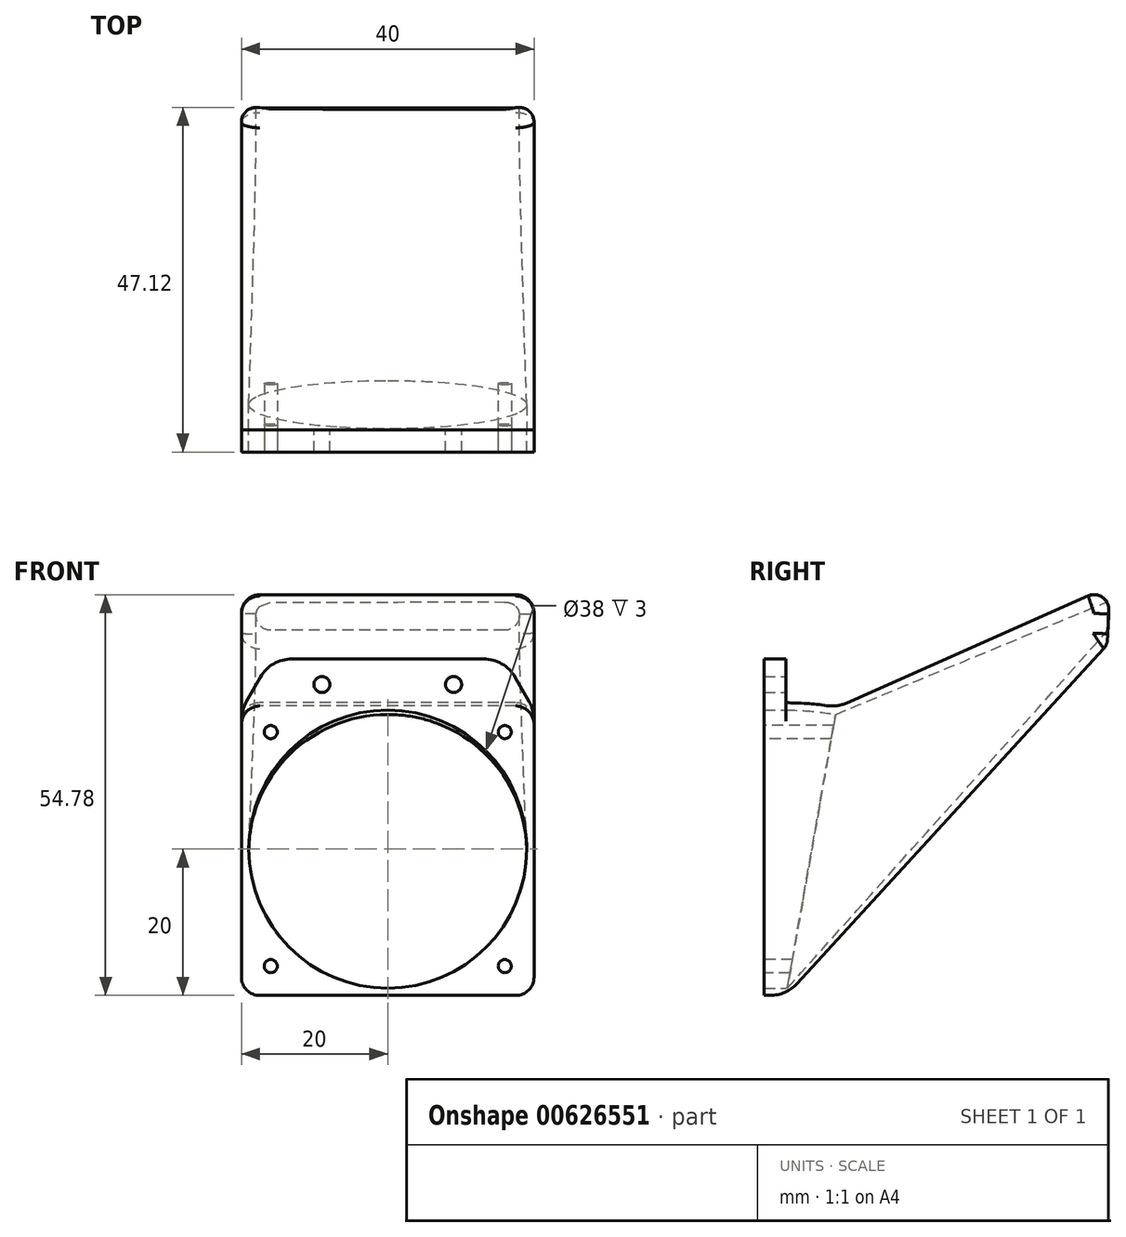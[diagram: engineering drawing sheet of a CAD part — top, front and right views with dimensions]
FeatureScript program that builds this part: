
annotation { "Feature Type Name" : "Feature", "Feature Type Description" : "" }
export const myFeature = defineFeature(function(context is Context, id is Id, definition is map)
    precondition{}
    {
        {
            var Q0;
            Q0=qCreatedBy(makeId("Front.planeOp"),FACE);
            var sketch = newSketch(context, id + "F0", { "sketchPlane" : qUnion([Q0])});
            skLineSegment(sketch, "E0.bottom", {"start": v(20, -23) * mm, "end": v(-20, -23) * mm});
            skLineSegment(sketch, "E0.top", {"start": v(20, 23) * mm, "end": v(-20, 23) * mm});
            skLineSegment(sketch, "E0.left", {"start": v(20, -23) * mm, "end": v(20, 23) * mm});
            skLineSegment(sketch, "E0.right", {"start": v(-20, -23) * mm, "end": v(-20, 23) * mm});
            skPoint(sketch, "E0.middle", {"position": v(0, 0) * mm});
            skSolve(sketch);
        }
        {
            var Q0;
            Q0=makeQuery(id+"F0.imprint","IMPRINT",FACE,{"disambiguationData":[TD([[makeQuery(id+"F0.imprint","IMPRINT",EDGE,{"derivedFrom":sQuery(id+"F0.wireOp",EDGE,"E0.bottom")}),-1.0]])]});
            extrude(context, id + "F1", {"entities" : qUnion([Q0]), "depth" : 3 * mm});
        }
        {
            var Q0;
            Q0=makeQuery(id+"F1.opExtrude","CAP_FACE",FACE,{"disambiguationData":[OSD([sQuery(id+"F0.wireOp",EDGE,"E0.bottom"),sQuery(id+"F0.wireOp",EDGE,"E0.top"),sQuery(id+"F0.wireOp",EDGE,"E0.left"),sQuery(id+"F0.wireOp",EDGE,"E0.right")])],"isStart":true});
            var sketch = newSketch(context, id + "F2", { "sketchPlane" : qUnion([Q0])});
            skLineSegment(sketch, "E1", {"start": v(0, 23) * mm, "end": v(0, -23) * mm, "construction": true});
            skLineSegment(sketch, "E2", {"start": v(-20, 19.5) * mm, "end": v(20, 19.5) * mm, "construction": true});
            skCircle(sketch, "E3", {"center": v(-9, 19.5) * mm, "radius": 1.1 * mm});
            skCircle(sketch, "E4", {"center": v(9, 19.5) * mm, "radius": 1.1 * mm});
            skCircle(sketch, "E5", {"center": v(0, -3) * mm, "radius": 19 * mm});
            skCircle(sketch, "E6", {"center": v(-15, 13) * mm, "radius": 1.1 * mm, "construction": true});
            skCircle(sketch, "E7", {"center": v(15, 13) * mm, "radius": 1.1 * mm, "construction": true});
            skCircle(sketch, "E8", {"center": v(15, -19) * mm, "radius": 1.1 * mm, "construction": true});
            skCircle(sketch, "E9", {"center": v(-15, -19) * mm, "radius": 1.1 * mm, "construction": true});
            skLineSegment(sketch, "E10", {"start": v(-20, -3) * mm, "end": v(20, -3) * mm, "construction": true});
            skLineSegment(sketch, "E11", {"start": v(-20, 17) * mm, "end": v(20, 17) * mm});
            skSolve(sketch);
        }
        {
            var Q0;
            Q0=makeQuery(id+"F2.imprint","IMPRINT",FACE,{"disambiguationData":[TD([[makeQuery(id+"F2.imprint","IMPRINT",EDGE,{"derivedFrom":sQuery(id+"F2.wireOp",EDGE,"E3")}),1.0]])]});
            var Q1;
            Q1=makeQuery(id+"F2.imprint","IMPRINT",FACE,{"disambiguationData":[TD([[makeQuery(id+"F2.imprint","IMPRINT",EDGE,{"derivedFrom":sQuery(id+"F2.wireOp",EDGE,"E4")}),1.0]])]});
            var Q2;
            Q2=makeQuery(id+"F2.imprint","IMPRINT",FACE,{"disambiguationData":[TD([[makeQuery(id+"F2.imprint","IMPRINT",EDGE,{"derivedFrom":sQuery(id+"F2.wireOp",EDGE,"E5")}),1.0]])]});
            extrude(context, id + "F3", {"entities" : qUnion([Q0, Q1, Q2]), "operationType" : NewBodyOperationType.REMOVE, "endBound" : BoundingType.UP_TO_NEXT, "oppositeDirection" : true, "depth" : 25 * mm});
        }
        {
            var Q0;
            Q0=makeQuery(id+"F1.opExtrude","SWEPT_FACE",FACE,{"disambiguationData":[OSD([sQuery(id+"F0.wireOp",EDGE,"E0.left")])]});
            cPlane(context, id + "F4", {"entities" : qUnion([Q0]), "cplaneType" : CPlaneType.OFFSET, "offset" : 0 * mm, "width" : 150 * mm, "height" : 150 * mm});
        }
        {
            var Q0;
            Q0=qCreatedBy(id+"F4.planeOp",FACE);
            var sketch = newSketch(context, id + "F5", { "sketchPlane" : qUnion([Q0])});
            skArc(sketch, "E12", {"start": v(6.95, 16.4) * mm, "mid": v(3.49, 16.85) * mm, "end": v(0, 17) * mm});
            skLineSegment(sketch, "E13", {"start": v(6.95, 16.4) * mm, "end": v(0, -23) * mm, "construction": true});
            skSolve(sketch);
        }
        {
            var Q0;
            Q0=makeQuery(id+"F2.imprint","IMPRINT",FACE,{"disambiguationData":[TD([[makeQuery(id+"F2.imprint","IMPRINT",EDGE,{"derivedFrom":sQuery(id+"F2.wireOp",EDGE,"E5")}),-1.0]])]});
            var Q1;
            Q1=sQuery(id+"F5.wireOp",EDGE,"E12");
            sweep(context, id + "F6", {"operationType" : NewBodyOperationType.ADD, "profiles" : qUnion([Q0]), "path" : qUnion([Q1])});
        }
        {
            var Q0;
            Q0=makeQuery(id+"F1.opExtrude","CAP_FACE",FACE,{"disambiguationData":[OSD([sQuery(id+"F0.wireOp",EDGE,"E0.bottom"),sQuery(id+"F0.wireOp",EDGE,"E0.top"),sQuery(id+"F0.wireOp",EDGE,"E0.left"),sQuery(id+"F0.wireOp",EDGE,"E0.right")])],"isStart":false});
            var sketch = newSketch(context, id + "F7", { "sketchPlane" : qUnion([Q0])});
            skCircle(sketch, "E14", {"center": v(-16, 13) * mm, "radius": 0.9 * mm});
            skCircle(sketch, "E15", {"center": v(16, 13) * mm, "radius": 0.9 * mm});
            skCircle(sketch, "E16", {"center": v(16, -19) * mm, "radius": 0.9 * mm});
            skCircle(sketch, "E17", {"center": v(-16, -19) * mm, "radius": 0.9 * mm});
            skLineSegment(sketch, "E18", {"start": v(0, -23) * mm, "end": v(0, 23) * mm, "construction": true});
            skLineSegment(sketch, "E19", {"start": v(-20, -3) * mm, "end": v(20, -3) * mm, "construction": true});
            skSolve(sketch);
        }
        {
            var Q0;
            Q0=makeQuery(id+"F7.imprint","IMPRINT",FACE,{"disambiguationData":[TD([[makeQuery(id+"F7.imprint","IMPRINT",EDGE,{"derivedFrom":sQuery(id+"F7.wireOp",EDGE,"E14")}),1.0]])]});
            var Q1;
            Q1=makeQuery(id+"F7.imprint","IMPRINT",FACE,{"disambiguationData":[TD([[makeQuery(id+"F7.imprint","IMPRINT",EDGE,{"derivedFrom":sQuery(id+"F7.wireOp",EDGE,"E15")}),1.0]])]});
            var Q2;
            Q2=makeQuery(id+"F7.imprint","IMPRINT",FACE,{"disambiguationData":[TD([[makeQuery(id+"F7.imprint","IMPRINT",EDGE,{"derivedFrom":sQuery(id+"F7.wireOp",EDGE,"E17")}),1.0]])]});
            var Q3;
            Q3=makeQuery(id+"F7.imprint","IMPRINT",FACE,{"disambiguationData":[TD([[makeQuery(id+"F7.imprint","IMPRINT",EDGE,{"derivedFrom":sQuery(id+"F7.wireOp",EDGE,"E16")}),1.0]])]});
            extrude(context, id + "F8", {"entities" : qUnion([Q0, Q1, Q2, Q3]), "operationType" : NewBodyOperationType.REMOVE, "oppositeDirection" : true, "depth" : 10 * mm});
        }
        {
            var Q0;
            Q0=qCreatedBy(id+"F4.planeOp",FACE);
            var sketch = newSketch(context, id + "F9", { "sketchPlane" : qUnion([Q0])});
            skLineSegment(sketch, "E20", {"start": v(0, -23) * mm, "end": v(43.91, 24.92) * mm});
            skLineSegment(sketch, "E21", {"start": v(43.91, 24.92) * mm, "end": v(44.26, 32.92) * mm});
            skLineSegment(sketch, "E22", {"start": v(44.26, 32.92) * mm, "end": v(6.95, 16.4) * mm});
            skLineSegment(sketch, "E23", {"start": v(0, -23) * mm, "end": v(6.95, 16.4) * mm});
            skSolve(sketch);
        }
        {
            var Q0;
            Q0=makeQuery(id+"F9.imprint","IMPRINT",FACE,{"disambiguationData":[TD([[makeQuery(id+"F9.imprint","IMPRINT",EDGE,{"derivedFrom":sQuery(id+"F9.wireOp",EDGE,"E20")}),1.0]])]});
            extrude(context, id + "F10", {"entities" : qUnion([Q0]), "operationType" : NewBodyOperationType.ADD, "oppositeDirection" : true, "depth" : 40 * mm, "offsetDistance" : 25 * mm});
        }
        {
            var Q0;
            Q0=makeQuery(id+"F10.opExtrude","SWEPT_FACE",FACE,{"disambiguationData":[OSD([sQuery(id+"F9.wireOp",EDGE,"E21")])]});
            var sketch = newSketch(context, id + "F11", { "sketchPlane" : qUnion([Q0])});
            skLineSegment(sketch, "E24", {"start": v(-16, 32.81) * mm, "end": v(16, 32.81) * mm});
            skLineSegment(sketch, "E25", {"start": v(-16, 28.81) * mm, "end": v(16, 28.81) * mm});
            skArc(sketch, "E26", {"start": v(-16, 32.81) * mm, "mid": v(-18, 30.81) * mm, "end": v(-16, 28.81) * mm});
            skArc(sketch, "E27", {"start": v(16, 28.81) * mm, "mid": v(18, 30.81) * mm, "end": v(16, 32.81) * mm});
            skSolve(sketch);
        }
        {
            var Q0;
            {var subQ0=sQuery(id+"F0.wireOp",EDGE,"E0.bottom");Q0=makeQuery(id+"F10.boolean.opBoolean","MERGE",EDGE,{"derivedFrom":[makeQuery(id+"F6.boolean.opBoolean","MERGE",EDGE,{"derivedFrom":[makeQuery(id+"F1.opExtrude","CAP_EDGE",EDGE,{"disambiguationData":[OSD([subQ0])],"isStart":true}),makeQuery(id+"F6.opSweep","CAP_EDGE",EDGE,{"disambiguationData":[OSD([subQ0,sQuery(id+"F5.wireOp",VERTEX,"E12.start"),sQuery(id+"F5.wireOp",VERTEX,"E12.end")])],"isStart":true})]}),makeQuery(id+"F10.opExtrude","SWEPT_EDGE",EDGE,{"disambiguationData":[OSD([sQuery(id+"F9.wireOp",EDGE,"E20"),sQuery(id+"F9.wireOp",EDGE,"E23")])]})]});}
            var Q1;
            Q1=makeQuery(id+"F10.boolean.opBoolean","MERGE",EDGE,{"derivedFrom":[makeQuery(id+"F6.opSweep","CAP_EDGE",EDGE,{"disambiguationData":[OSD([sQuery(id+"F2.wireOp",EDGE,"E11"),sQuery(id+"F5.wireOp",VERTEX,"E12.start")])],"isStart":false}),makeQuery(id+"F10.opExtrude","SWEPT_EDGE",EDGE,{"disambiguationData":[OSD([sQuery(id+"F9.wireOp",EDGE,"E22"),sQuery(id+"F9.wireOp",EDGE,"E23")])]})]});
            fillet(context, id + "F12", {"entities" : qUnion([Q0, Q1]), "radius" : 5 * mm, "tangentPropagation" : true, "allowEdgeOverflow" : false});
        }
        {
            var Q0;
            Q0=makeQuery(id+"F10.opExtrude","CAP_EDGE",EDGE,{"disambiguationData":[OSD([sQuery(id+"F9.wireOp",EDGE,"E20")])],"isStart":true});
            var Q1;
            Q1=makeQuery(id+"F10.opExtrude","CAP_EDGE",EDGE,{"disambiguationData":[OSD([sQuery(id+"F9.wireOp",EDGE,"E22")])],"isStart":true});
            var Q2;
            Q2=makeQuery(id+"F10.opExtrude","CAP_EDGE",EDGE,{"disambiguationData":[OSD([sQuery(id+"F9.wireOp",EDGE,"E22")])],"isStart":false});
            var Q3;
            Q3=makeQuery(id+"F10.opExtrude","CAP_EDGE",EDGE,{"disambiguationData":[OSD([sQuery(id+"F9.wireOp",EDGE,"E20")])],"isStart":false});
            fillet(context, id + "F13", {"entities" : qUnion([Q0, Q1, Q2, Q3]), "radius" : 2.5 * mm, "tangentPropagation" : true, "allowEdgeOverflow" : false});
        }
        {
            var Q1;
            Q1=makeQuery(id+"F11.imprint","IMPRINT",FACE,{"disambiguationData":[TD([[makeQuery(id+"F11.imprint","IMPRINT",EDGE,{"derivedFrom":sQuery(id+"F11.wireOp",EDGE,"E24")}),-1.0]])]});
            var Q2;
            Q2=makeQuery(id+"F10.boolean.opBoolean","SPLIT",FACE,{"disambiguationData":[TD([makeQuery(id+"F6.opSweep","SWEPT_FACE",FACE,{"disambiguationData":[OSD([sQuery(id+"F2.wireOp",EDGE,"E5"),sQuery(id+"F5.wireOp",EDGE,"E12")])]})])],"derivedFrom":makeQuery(id+"F10.opExtrude","SWEPT_FACE",FACE,{"disambiguationData":[OSD([sQuery(id+"F9.wireOp",EDGE,"E23")])]})});
            loft(context, id + "F14", {"operationType" : NewBodyOperationType.REMOVE, "sheetProfilesArray" : [{ "sheetProfileEntities" : qUnion([Q1]) }, { "sheetProfileEntities" : qUnion([Q2]) }]});
        }
        {
            var Q0;
            Q0=makeQuery(id+"F1.opExtrude","SWEPT_EDGE",EDGE,{"disambiguationData":[OSD([sQuery(id+"F0.wireOp",EDGE,"E0.top"),sQuery(id+"F0.wireOp",EDGE,"E0.right")])]});
            var Q1;
            Q1=makeQuery(id+"F1.opExtrude","SWEPT_EDGE",EDGE,{"disambiguationData":[OSD([sQuery(id+"F0.wireOp",EDGE,"E0.top"),sQuery(id+"F0.wireOp",EDGE,"E0.left")])]});
            chamfer(context, id + "F15", {"entities" : qUnion([Q0, Q1]), "chamferType" : ChamferType.TWO_OFFSETS, "width1" : 7 * mm, "oppositeDirection" : false, "width2" : 4 * mm, "tangentPropagation" : true});
        }
        {
            var Q0;
            {var subQ0=sQuery(id+"F0.wireOp",EDGE,"E0.top");Q0=makeQuery(id+"F15.opChamfer","BLEND_EDGE",EDGE,{"blendedFrom":[makeQuery(id+"F1.opExtrude","SWEPT_EDGE",EDGE,{"disambiguationData":[OSD([subQ0,sQuery(id+"F0.wireOp",EDGE,"E0.right")])]}),makeQuery(id+"F1.opExtrude","SWEPT_FACE",FACE,{"disambiguationData":[OSD([subQ0])]})],"blendedInto":[makeQuery(id+"F1.opExtrude","SWEPT_FACE",FACE,{"disambiguationData":[OSD([subQ0])]})]});}
            var Q1;
            {var subQ0=sQuery(id+"F0.wireOp",EDGE,"E0.right");Q1=makeQuery(id+"F15.opChamfer","BLEND_EDGE",EDGE,{"blendedFrom":[makeQuery(id+"F1.opExtrude","SWEPT_EDGE",EDGE,{"disambiguationData":[OSD([sQuery(id+"F0.wireOp",EDGE,"E0.top"),subQ0])]}),makeQuery(id+"F10.boolean.opBoolean","MERGE",FACE,{"derivedFrom":[makeQuery(id+"F6.boolean.opBoolean","MERGE",FACE,{"derivedFrom":[makeQuery(id+"F1.opExtrude","SWEPT_FACE",FACE,{"disambiguationData":[OSD([subQ0])]}),makeQuery(id+"F6.opSweep","SWEPT_FACE",FACE,{"disambiguationData":[OSD([subQ0,sQuery(id+"F5.wireOp",EDGE,"E12")])]})]}),makeQuery(id+"F10.opExtrude","CAP_FACE",FACE,{"disambiguationData":[OSD([sQuery(id+"F9.wireOp",EDGE,"E20"),sQuery(id+"F9.wireOp",EDGE,"E21"),sQuery(id+"F9.wireOp",EDGE,"E22"),sQuery(id+"F9.wireOp",EDGE,"E23")])],"isStart":false})]})],"blendedInto":[makeQuery(id+"F10.boolean.opBoolean","MERGE",FACE,{"derivedFrom":[makeQuery(id+"F6.boolean.opBoolean","MERGE",FACE,{"derivedFrom":[makeQuery(id+"F1.opExtrude","SWEPT_FACE",FACE,{"disambiguationData":[OSD([subQ0])]}),makeQuery(id+"F6.opSweep","SWEPT_FACE",FACE,{"disambiguationData":[OSD([subQ0,sQuery(id+"F5.wireOp",EDGE,"E12")])]})]}),makeQuery(id+"F10.opExtrude","CAP_FACE",FACE,{"disambiguationData":[OSD([sQuery(id+"F9.wireOp",EDGE,"E20"),sQuery(id+"F9.wireOp",EDGE,"E21"),sQuery(id+"F9.wireOp",EDGE,"E22"),sQuery(id+"F9.wireOp",EDGE,"E23")])],"isStart":false})]})]});}
            var Q2;
            {var subQ0=sQuery(id+"F0.wireOp",EDGE,"E0.left");Q2=makeQuery(id+"F15.opChamfer","BLEND_EDGE",EDGE,{"blendedFrom":[makeQuery(id+"F1.opExtrude","SWEPT_EDGE",EDGE,{"disambiguationData":[OSD([sQuery(id+"F0.wireOp",EDGE,"E0.top"),subQ0])]}),makeQuery(id+"F10.boolean.opBoolean","MERGE",FACE,{"derivedFrom":[makeQuery(id+"F6.boolean.opBoolean","MERGE",FACE,{"derivedFrom":[makeQuery(id+"F1.opExtrude","SWEPT_FACE",FACE,{"disambiguationData":[OSD([subQ0])]}),makeQuery(id+"F6.opSweep","SWEPT_FACE",FACE,{"disambiguationData":[OSD([subQ0,sQuery(id+"F5.wireOp",EDGE,"E12")])]})]}),makeQuery(id+"F10.opExtrude","CAP_FACE",FACE,{"disambiguationData":[OSD([sQuery(id+"F9.wireOp",EDGE,"E20"),sQuery(id+"F9.wireOp",EDGE,"E21"),sQuery(id+"F9.wireOp",EDGE,"E22"),sQuery(id+"F9.wireOp",EDGE,"E23")])],"isStart":true})]})],"blendedInto":[makeQuery(id+"F10.boolean.opBoolean","MERGE",FACE,{"derivedFrom":[makeQuery(id+"F6.boolean.opBoolean","MERGE",FACE,{"derivedFrom":[makeQuery(id+"F1.opExtrude","SWEPT_FACE",FACE,{"disambiguationData":[OSD([subQ0])]}),makeQuery(id+"F6.opSweep","SWEPT_FACE",FACE,{"disambiguationData":[OSD([subQ0,sQuery(id+"F5.wireOp",EDGE,"E12")])]})]}),makeQuery(id+"F10.opExtrude","CAP_FACE",FACE,{"disambiguationData":[OSD([sQuery(id+"F9.wireOp",EDGE,"E20"),sQuery(id+"F9.wireOp",EDGE,"E21"),sQuery(id+"F9.wireOp",EDGE,"E22"),sQuery(id+"F9.wireOp",EDGE,"E23")])],"isStart":true})]})]});}
            var Q3;
            {var subQ0=sQuery(id+"F0.wireOp",EDGE,"E0.top");Q3=makeQuery(id+"F15.opChamfer","BLEND_EDGE",EDGE,{"blendedFrom":[makeQuery(id+"F1.opExtrude","SWEPT_EDGE",EDGE,{"disambiguationData":[OSD([subQ0,sQuery(id+"F0.wireOp",EDGE,"E0.left")])]}),makeQuery(id+"F1.opExtrude","SWEPT_FACE",FACE,{"disambiguationData":[OSD([subQ0])]})],"blendedInto":[makeQuery(id+"F1.opExtrude","SWEPT_FACE",FACE,{"disambiguationData":[OSD([subQ0])]})]});}
            fillet(context, id + "F16", {"entities" : qUnion([Q0, Q1, Q2, Q3]), "radius" : 5 * mm, "tangentPropagation" : true, "allowEdgeOverflow" : false});
        }
        {
            var Q0;
            Q0=makeQuery(id+"F13.opFillet","BLEND_EDGE",EDGE,{"blendedFrom":[makeQuery(id+"F10.opExtrude","CAP_EDGE",EDGE,{"disambiguationData":[OSD([sQuery(id+"F9.wireOp",EDGE,"E20")])],"isStart":true}),makeQuery(id+"F10.opExtrude","SWEPT_FACE",FACE,{"disambiguationData":[OSD([sQuery(id+"F9.wireOp",EDGE,"E21")])]})],"blendedInto":[makeQuery(id+"F10.opExtrude","SWEPT_FACE",FACE,{"disambiguationData":[OSD([sQuery(id+"F9.wireOp",EDGE,"E21")])]})]});
            var Q1;
            Q1=makeQuery(id+"F10.opExtrude","SWEPT_EDGE",EDGE,{"disambiguationData":[OSD([sQuery(id+"F9.wireOp",EDGE,"E21"),sQuery(id+"F9.wireOp",EDGE,"E22")])]});
            fillet(context, id + "F17", {"entities" : qUnion([Q0, Q1]), "radius" : 2 * mm, "tangentPropagation" : true, "allowEdgeOverflow" : false});
        }
    });
